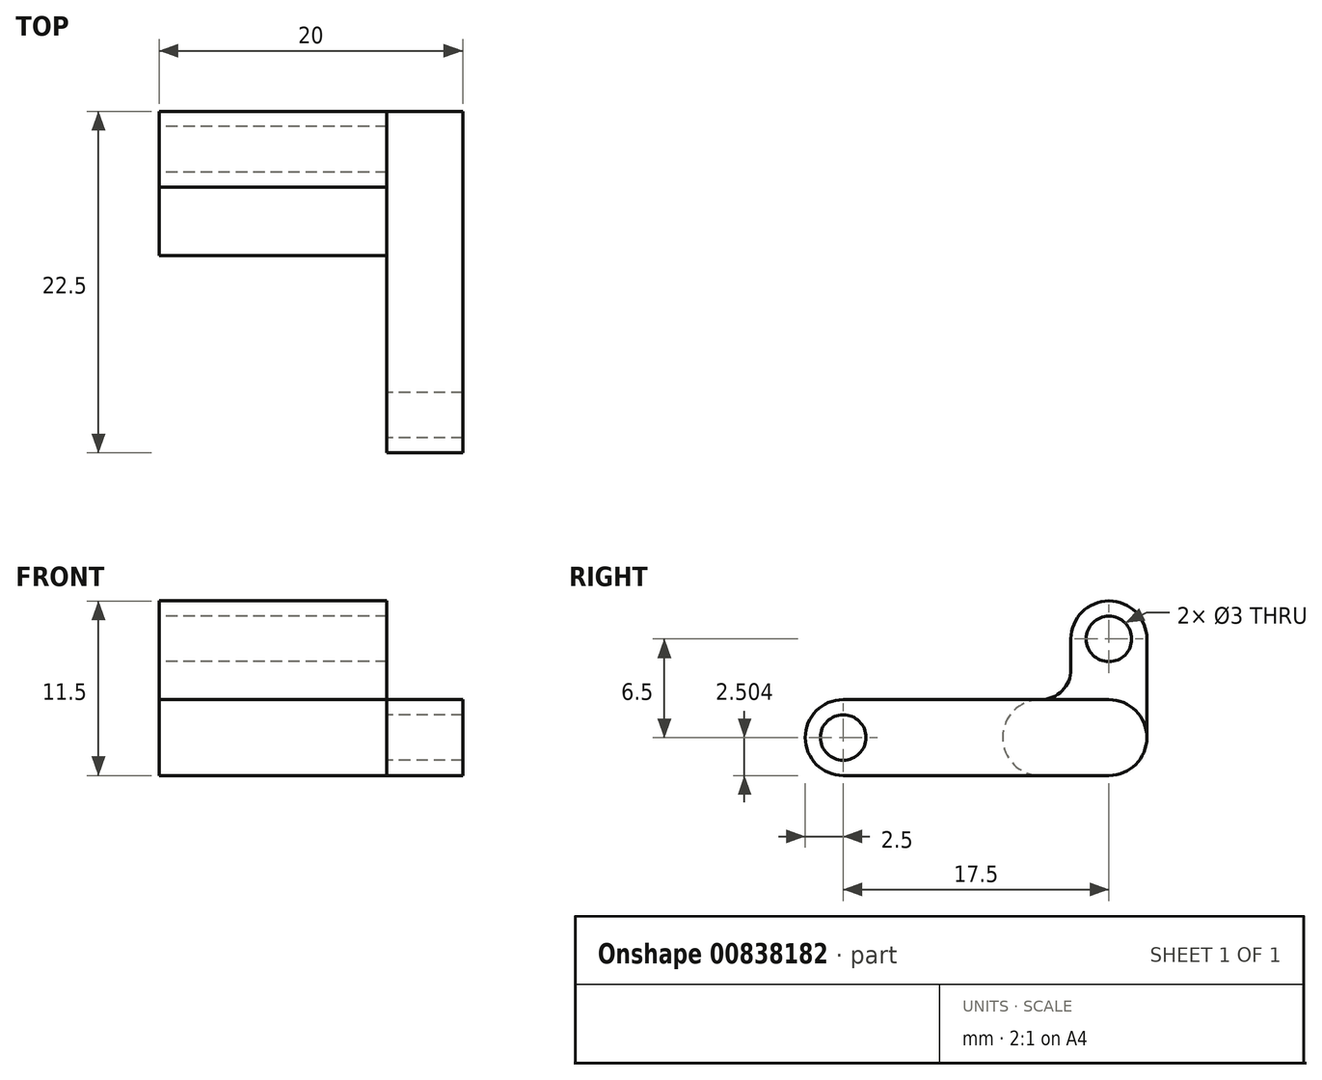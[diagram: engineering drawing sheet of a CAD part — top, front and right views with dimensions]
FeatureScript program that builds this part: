
annotation { "Feature Type Name" : "Feature", "Feature Type Description" : "" }
export const myFeature = defineFeature(function(context is Context, id is Id, definition is map)
    precondition{}
    {
        {
            var Q0;
            Q0=qCreatedBy(makeId("Right.planeOp"),FACE);
            var sketch = newSketch(context, id + "F0", { "sketchPlane" : qUnion([Q0])});
            skLineSegment(sketch, "E0.top", {"start": v(-2.5, -0.69) * mm, "end": v(2.5, -0.69) * mm});
            skLineSegment(sketch, "E0.left", {"start": v(-2.5, 8.31) * mm, "end": v(-2.5, 6.31) * mm});
            skLineSegment(sketch, "E0.right", {"start": v(2.5, 8.31) * mm, "end": v(2.5, -0.69) * mm});
            skArc(sketch, "E1", {"start": v(2.5, 8.31) * mm, "mid": v(0, 10.81) * mm, "end": v(-2.5, 8.31) * mm});
            skLineSegment(sketch, "E2.bottom", {"start": v(-2.5, -0.69) * mm, "end": v(-4.5, -0.69) * mm});
            skLineSegment(sketch, "E2.top", {"start": v(-4.5, 4.31) * mm, "end": v(-4.5, 4.31) * mm});
            skArc(sketch, "E3", {"start": v(-4.5, 4.31) * mm, "mid": v(-7, 1.81) * mm, "end": v(-4.5, -0.69) * mm});
            skPoint(sketch, "E3.centerSnap0", {"position": v(-7, 1.81) * mm});
            skPoint(sketch, "E4.orphan", {"position": v(-2.5, 10.81) * mm});
            skPoint(sketch, "E5.orphan", {"position": v(2.5, 10.81) * mm});
            skPoint(sketch, "E6.orphan", {"position": v(-7, 4.31) * mm});
            skPoint(sketch, "E7.orphan", {"position": v(-7, -0.69) * mm});
            skPoint(sketch, "E8.visualSharp", {"position": v(-2.5, 4.31) * mm});
            skArc(sketch, "E8.filletArc", {"start": v(-4.5, 4.31) * mm, "mid": v(-3.09, 4.9) * mm, "end": v(-2.5, 6.31) * mm});
            skCircle(sketch, "E9", {"center": v(0, 8.31) * mm, "radius": 1.5 * mm});
            skSolve(sketch);
        }
        {
            var Q0;
            Q0 = qSketchRegion(id + "F0", true);
            extrude(context, id + "F1", {"entities" : qUnion([Q0]), "endBound" : BoundingType.SYMMETRIC, "depth" : 15 * mm, "offsetDistance" : 25 * mm});
        }
        {
            var Q0;
            Q0=makeQuery(id+"F1.opExtrude","CAP_FACE",FACE,{"disambiguationData":[OSD([sQuery(id+"F0.wireOp",EDGE,"E0.top"),sQuery(id+"F0.wireOp",EDGE,"E0.left"),sQuery(id+"F0.wireOp",EDGE,"E0.right"),sQuery(id+"F0.wireOp",EDGE,"E1"),sQuery(id+"F0.wireOp",EDGE,"E2.bottom"),sQuery(id+"F0.wireOp",EDGE,"E3"),sQuery(id+"F0.wireOp",EDGE,"E8.filletArc"),sQuery(id+"F0.wireOp",EDGE,"E9")])],"isStart":false});
            var sketch = newSketch(context, id + "F2", { "sketchPlane" : qUnion([Q0])});
            skLineSegment(sketch, "E10.bottom", {"start": v(0, -0.69) * mm, "end": v(-17.5, -0.69) * mm});
            skLineSegment(sketch, "E10.top", {"start": v(0, 4.31) * mm, "end": v(-17.5, 4.31) * mm});
            skArc(sketch, "E11", {"start": v(-17.5, 4.31) * mm, "mid": v(-20, 1.81) * mm, "end": v(-17.5, -0.69) * mm});
            skPoint(sketch, "E11.centerSnap0", {"position": v(-20, 1.81) * mm});
            skArc(sketch, "E12", {"start": v(0, -0.69) * mm, "mid": v(2.5, 1.81) * mm, "end": v(0, 4.31) * mm});
            skPoint(sketch, "E12.centerSnap0", {"position": v(2.5, 1.81) * mm});
            skPoint(sketch, "E13.orphan", {"position": v(-20, 4.31) * mm});
            skPoint(sketch, "E10.left.end.orphan", {"position": v(2.5, 4.31) * mm});
            skPoint(sketch, "E14.orphan", {"position": v(2.5, -0.69) * mm});
            skPoint(sketch, "E15.orphan", {"position": v(-20, -0.69) * mm});
            skCircle(sketch, "E16", {"center": v(-17.5, 1.81) * mm, "radius": 1.5 * mm});
            skSolve(sketch);
        }
        {
            var Q0;
            Q0 = qSketchRegion(id + "F2", true);
            extrude(context, id + "F3", {"entities" : qUnion([Q0]), "operationType" : NewBodyOperationType.ADD, "depth" : 5 * mm, "offsetDistance" : 25 * mm});
        }
        {
            var Q0;
            Q0=makeQuery(id+"F1.opExtrude","SWEPT_EDGE",EDGE,{"disambiguationData":[OSD([sQuery(id+"F0.wireOp",EDGE,"E0.top"),sQuery(id+"F0.wireOp",EDGE,"E0.right")])]});
            fillet(context, id + "F4", {"entities" : qUnion([Q0]), "radius" : 2.5 * mm, "tangentPropagation" : true, "allowEdgeOverflow" : false});
        }
    });
